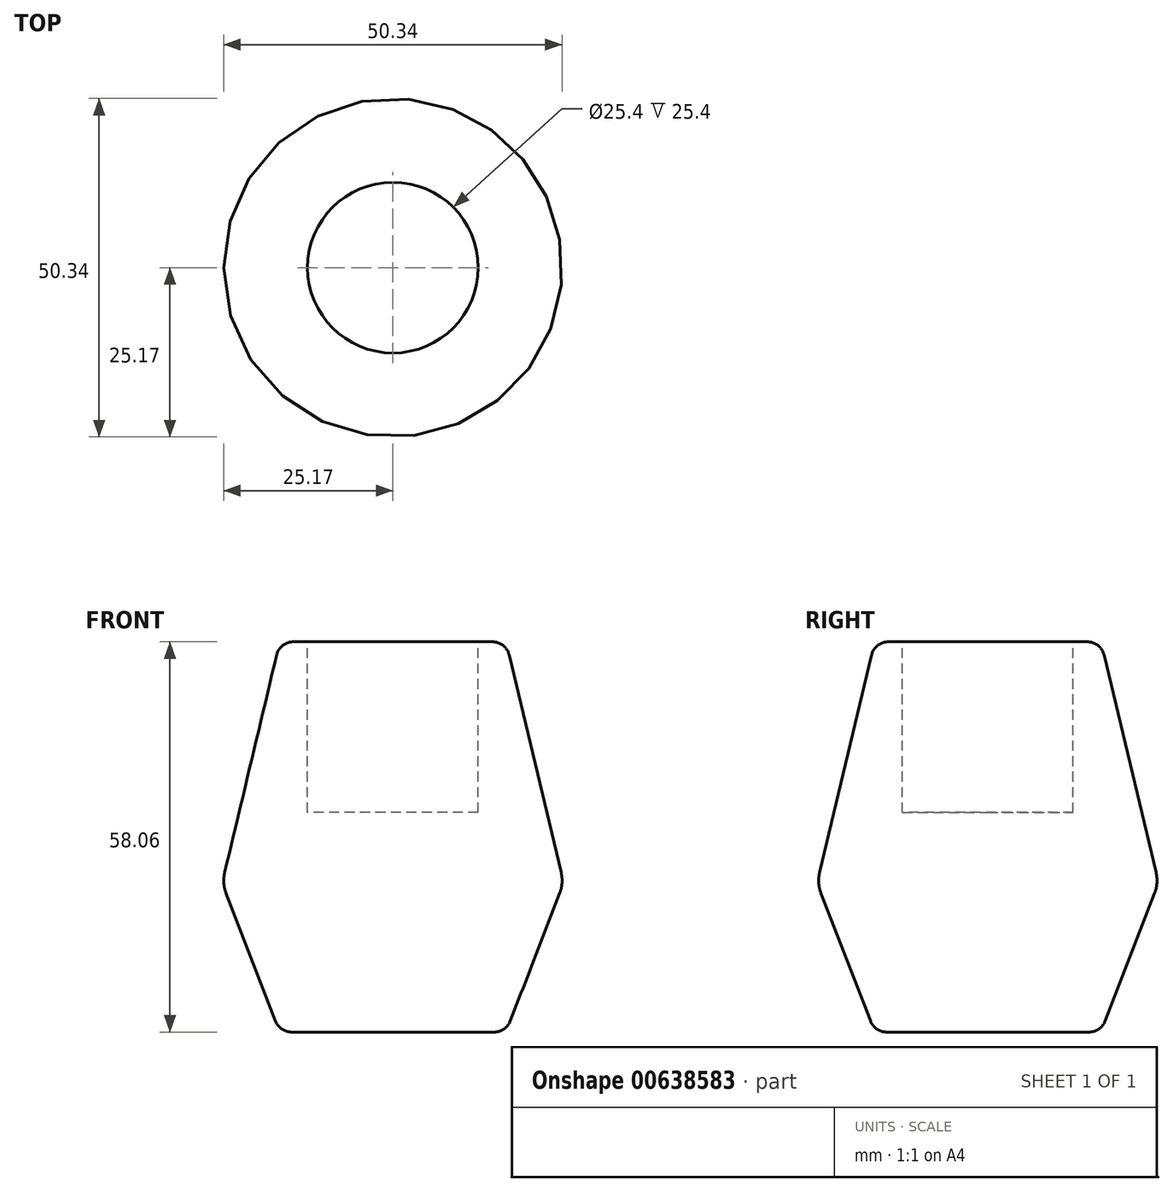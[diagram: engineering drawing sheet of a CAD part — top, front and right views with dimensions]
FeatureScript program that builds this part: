
annotation { "Feature Type Name" : "Feature", "Feature Type Description" : "" }
export const myFeature = defineFeature(function(context is Context, id is Id, definition is map)
    precondition{}
    {
        {
            var Q0;
            Q0=qCreatedBy(makeId("Front.planeOp"),FACE);
            var sketch = newSketch(context, id + "F0", { "sketchPlane" : qUnion([Q0])});
            skLineSegment(sketch, "E0", {"start": v(0, 0) * mm, "end": v(0, 58.06) * mm});
            skLineSegment(sketch, "E1", {"start": v(0, 58.06) * mm, "end": v(-16.83, 58.06) * mm});
            skLineSegment(sketch, "E2", {"start": v(0, 58.06) * mm, "end": v(0, 22.17) * mm});
            skLineSegment(sketch, "E3", {"start": v(0, 22.17) * mm, "end": v(-25.4, 22.17) * mm});
            skLineSegment(sketch, "E4", {"start": v(-25.4, 22.17) * mm, "end": v(-16.83, 58.06) * mm});
            skLineSegment(sketch, "E5", {"start": v(-16.83, 58.06) * mm, "end": v(-16.83, 0) * mm});
            skLineSegment(sketch, "E6", {"start": v(-16.83, 0) * mm, "end": v(0, 0) * mm});
            skLineSegment(sketch, "E7", {"start": v(-25.4, 22.17) * mm, "end": v(-16.83, 0) * mm});
            skSolve(sketch);
        }
        {
            var Q0;
            Q0 = qSketchRegion(id + "F0", true);
            var Q1;
            Q1=sQuery(id+"F0.wireOp",EDGE,"E2");
            revolve(context, id + "F1", {"entities" : qUnion([Q0]), "axis" : qUnion([Q1]), "revolveType" : RevolveType.FULL});
        }
        {
            var Q0;
            Q0=makeQuery(id+"F1.opRevolve","SWEPT_EDGE",EDGE,{"disambiguationData":[OSD([sQuery(id+"F0.wireOp",EDGE,"E3"),sQuery(id+"F0.wireOp",EDGE,"E4"),sQuery(id+"F0.wireOp",EDGE,"E7")])]});
            fillet(context, id + "F2", {"entities" : qUnion([Q0]), "radius" : 5.08 * mm, "tangentPropagation" : true, "allowEdgeOverflow" : false});
        }
        {
            var Q0;
            Q0=makeQuery(id+"F1.opRevolve","SWEPT_FACE",FACE,{"disambiguationData":[OSD([sQuery(id+"F0.wireOp",EDGE,"E7")])]});
            fillet(context, id + "F3", {"entities" : qUnion([Q0]), "radius" : 2.54 * mm, "tangentPropagation" : true, "allowEdgeOverflow" : false});
        }
        {
            var Q0;
            Q0=makeQuery(id+"F1.opRevolve","SWEPT_EDGE",EDGE,{"disambiguationData":[OSD([sQuery(id+"F0.wireOp",EDGE,"E1"),sQuery(id+"F0.wireOp",EDGE,"E4"),sQuery(id+"F0.wireOp",EDGE,"E5")])]});
            fillet(context, id + "F4", {"entities" : qUnion([Q0]), "radius" : 2.54 * mm, "tangentPropagation" : true, "allowEdgeOverflow" : false});
        }
        {
            var Q0;
            Q0=makeQuery(id+"F1.opRevolve","SWEPT_FACE",FACE,{"disambiguationData":[OSD([sQuery(id+"F0.wireOp",EDGE,"E1")])]});
            var sketch = newSketch(context, id + "F5", { "sketchPlane" : qUnion([Q0])});
            skCircle(sketch, "E8", {"center": v(0, 0) * mm, "radius": 12.7 * mm});
            skSolve(sketch);
        }
        {
            var Q0;
            Q0 = qSketchRegion(id + "F5", true);
            extrude(context, id + "F6", {"entities" : qUnion([Q0]), "operationType" : NewBodyOperationType.REMOVE, "oppositeDirection" : true, "depth" : 25.4 * mm, "offsetDistance" : 25.4 * mm});
        }
    });
